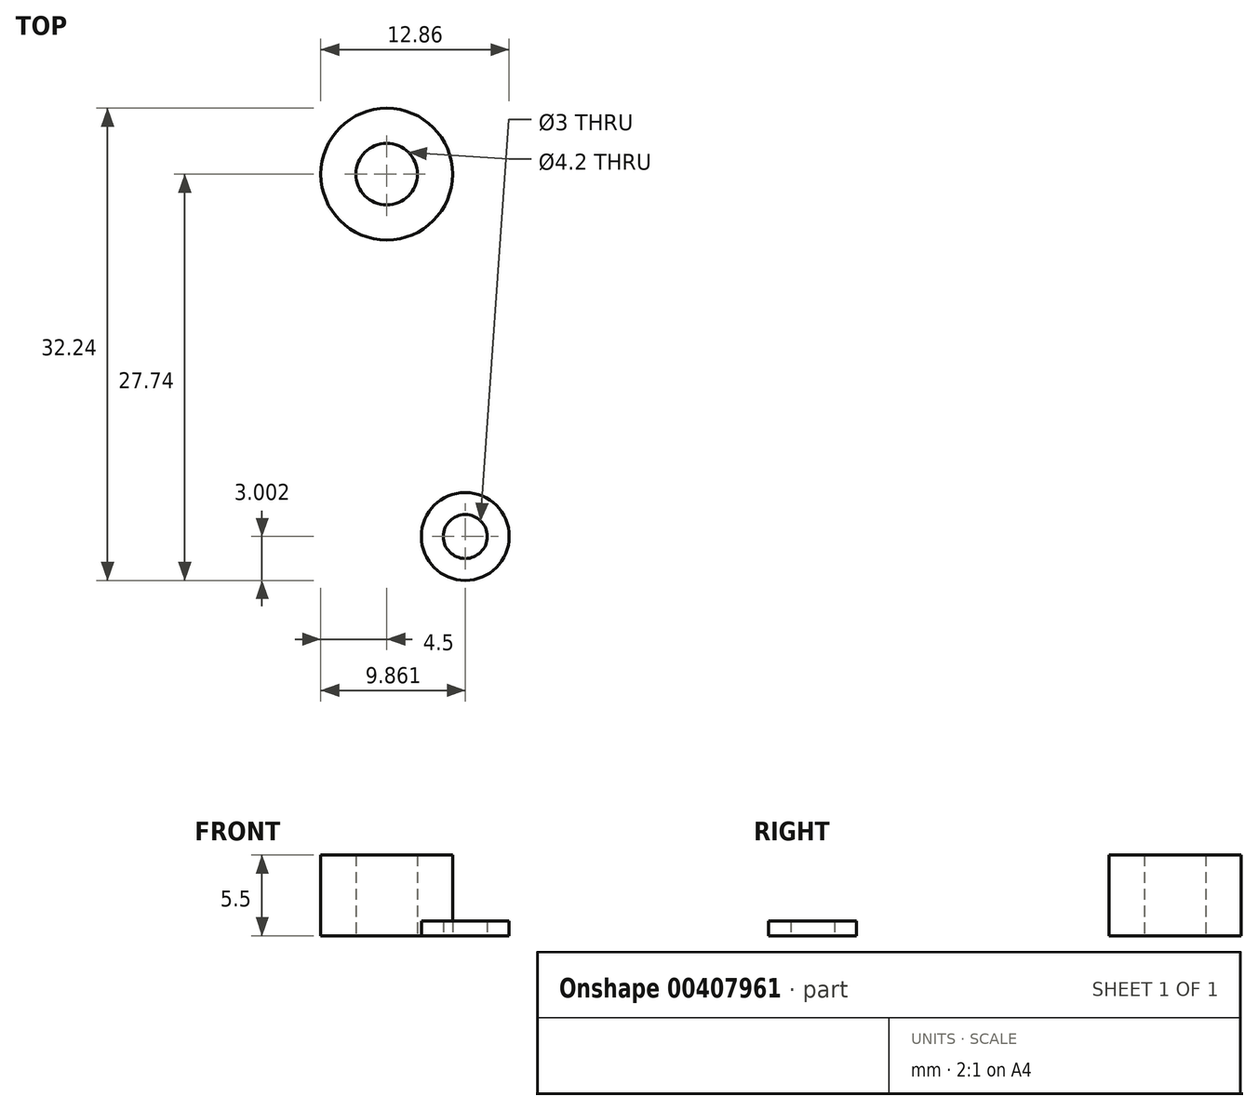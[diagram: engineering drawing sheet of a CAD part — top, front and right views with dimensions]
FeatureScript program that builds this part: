
annotation { "Feature Type Name" : "Feature", "Feature Type Description" : "" }
export const myFeature = defineFeature(function(context is Context, id is Id, definition is map)
    precondition{}
    {
        {
            var Q0;
            Q0=qCreatedBy(makeId("Top.planeOp"),FACE);
            var sketch = newSketch(context, id + "F0", { "sketchPlane" : qUnion([Q0])});
            skCircle(sketch, "E0", {"center": v(0, 0) * mm, "radius": 4.5 * mm});
            skCircle(sketch, "E1", {"center": v(0, 0) * mm, "radius": 2.1 * mm});
            skSolve(sketch);
        }
        {
            var Q0;
            Q0=makeQuery(id+"F0.imprint","IMPRINT",FACE,{"disambiguationData":[TD([[makeQuery(id+"F0.imprint","IMPRINT",EDGE,{"derivedFrom":sQuery(id+"F0.wireOp",EDGE,"E0")}),1.0]])]});
            extrude(context, id + "F1", {"entities" : qUnion([Q0]), "offsetDistance" : 25.4 * mm, "depth" : 5.5 * mm});
        }
        {
            var Q0;
            Q0=qCreatedBy(makeId("Top.planeOp"),FACE);
            var sketch = newSketch(context, id + "F2", { "sketchPlane" : qUnion([Q0])});
            skCircle(sketch, "E2", {"center": v(5.36, -24.74) * mm, "radius": 1.5 * mm});
            skCircle(sketch, "E3.0", {"center": v(5.36, -24.74) * mm, "radius": 3 * mm});
            skSolve(sketch);
        }
        {
            var Q0;
            Q0=makeQuery(id+"F2.imprint","IMPRINT",FACE,{"disambiguationData":[TD([[makeQuery(id+"F2.imprint","IMPRINT",EDGE,{"derivedFrom":sQuery(id+"F2.wireOp",EDGE,"E2")}),-1.0]])]});
            extrude(context, id + "F3", {"entities" : qUnion([Q0]), "depth" : 1 * mm, "offsetDistance" : 25.4 * mm});
        }
    });
